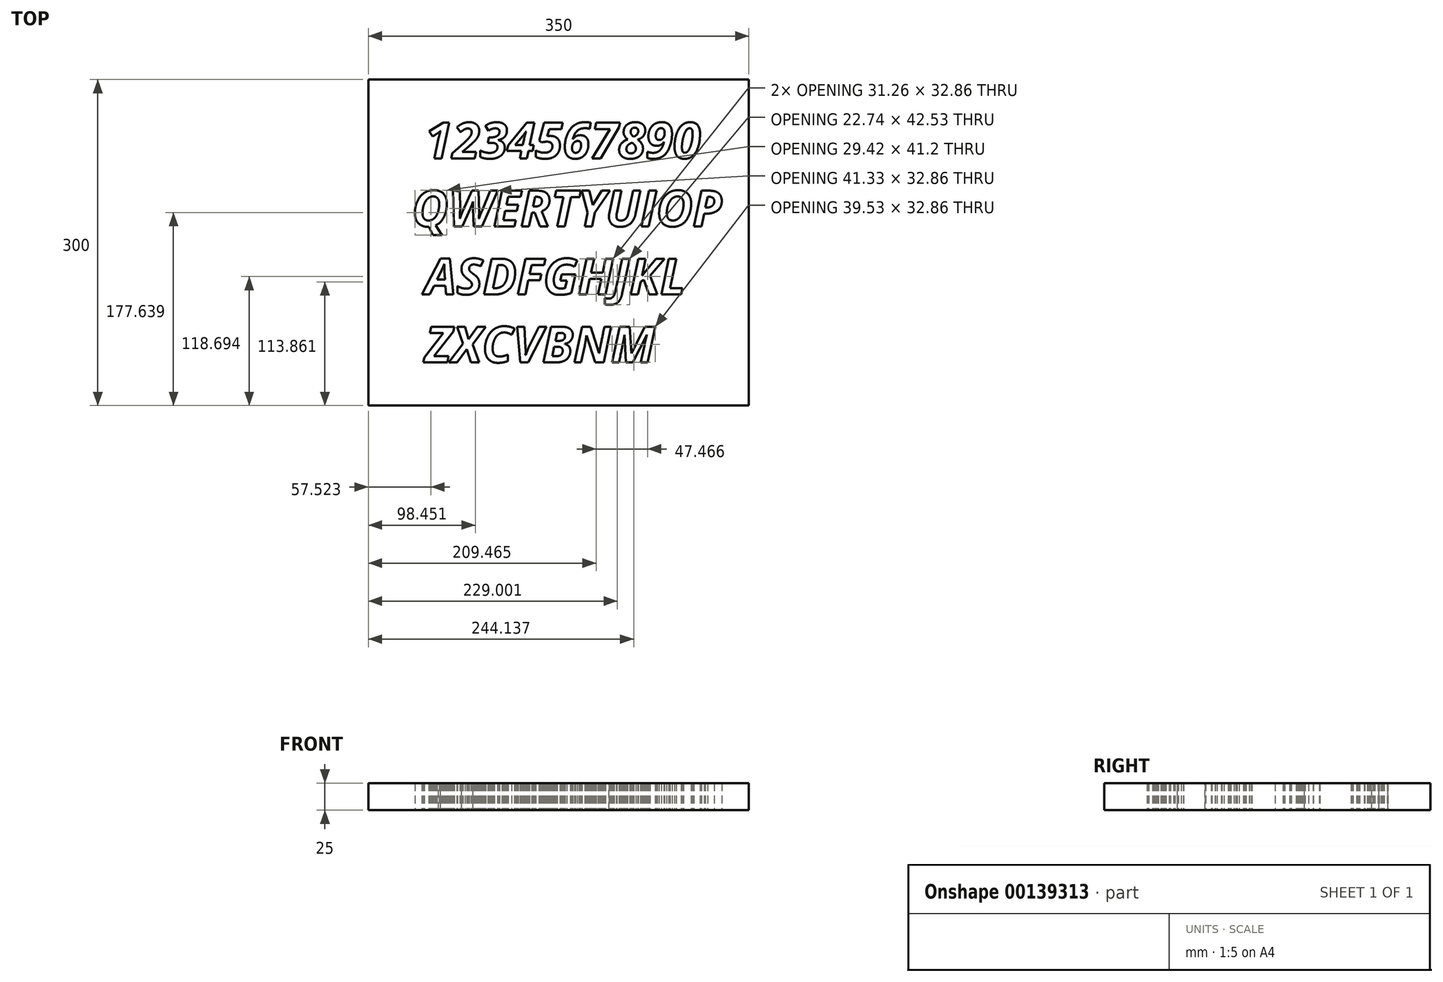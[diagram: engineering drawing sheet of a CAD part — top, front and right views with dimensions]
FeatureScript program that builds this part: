
annotation { "Feature Type Name" : "Feature", "Feature Type Description" : "" }
export const myFeature = defineFeature(function(context is Context, id is Id, definition is map)
    precondition{}
    {
        {
            var Q0;
            Q0=qCreatedBy(makeId("Top.planeOp"),FACE);
            var sketch = newSketch(context, id + "F0", { "sketchPlane" : qUnion([Q0])});
            skText(sketch, "E0", { "text": "  1234567890\n QWERTYUIOP\n  ASDFGHJKL\n  ZXCVBNM", "fontName": "OpenSans-BoldItalic.ttf"});
            const initialGuessF0  = {"E0": [-0.02613, -0.01612, 1, 0, 0.03314]};
            skSetInitialGuess(sketch, initialGuessF0);
            skSolve(sketch);
        }
        {
            var Q0;
            Q0 = qSketchRegion(id + "F0", true);
            extrude(context, id + "F1", {"entities" : qUnion([Q0]), "depth" : 25 * mm});
        }
        {
            var Q0;
            Q0=qCreatedBy(makeId("Top.planeOp"),FACE);
            var sketch = newSketch(context, id + "F2", { "sketchPlane" : qUnion([Q0])});
            skLineSegment(sketch, "E1.bottom", {"start": v(-54.22, 56.42) * mm, "end": v(295.78, 56.42) * mm});
            skLineSegment(sketch, "E1.top", {"start": v(-54.22, -243.58) * mm, "end": v(295.78, -243.58) * mm});
            skLineSegment(sketch, "E1.left", {"start": v(-54.22, 56.42) * mm, "end": v(-54.22, -243.58) * mm});
            skLineSegment(sketch, "E1.right", {"start": v(295.78, 56.42) * mm, "end": v(295.78, -243.58) * mm});
            skSolve(sketch);
        }
        {
            var Q0;
            Q0=makeQuery(id+"F2.imprint","IMPRINT",FACE,{"disambiguationData":[TD([[makeQuery(id+"F2.imprint","IMPRINT",EDGE,{"derivedFrom":sQuery(id+"F2.wireOp",EDGE,"E1.bottom")}),-1.0]])]});
            extrude(context, id + "F3", {"entities" : qUnion([Q0]), "depth" : 25 * mm});
        }
        {
            var Q0;
            Q0=makeQuery(id+"F1.opExtrude","SWEPT_BODY",BODY,{"disambiguationData":[OSD([sQuery(id+"F0.wireOp",EDGE,"E0.sketch_text.stroke-0"),sQuery(id+"F0.wireOp",EDGE,"E0.sketch_text.stroke-1"),sQuery(id+"F0.wireOp",EDGE,"E0.sketch_text.stroke-2"),sQuery(id+"F0.wireOp",EDGE,"E0.sketch_text.stroke-3"),sQuery(id+"F0.wireOp",EDGE,"E0.sketch_text.stroke-4"),sQuery(id+"F0.wireOp",EDGE,"E0.sketch_text.stroke-5"),sQuery(id+"F0.wireOp",EDGE,"E0.sketch_text.stroke-6"),sQuery(id+"F0.wireOp",EDGE,"E0.sketch_text.stroke-7"),sQuery(id+"F0.wireOp",EDGE,"E0.sketch_text.stroke-8")])]});
            var Q1;
            Q1=makeQuery(id+"F1.opExtrude","SWEPT_BODY",BODY,{"disambiguationData":[OSD([sQuery(id+"F0.wireOp",EDGE,"E0.sketch_text.stroke-9"),sQuery(id+"F0.wireOp",EDGE,"E0.sketch_text.stroke-10"),sQuery(id+"F0.wireOp",EDGE,"E0.sketch_text.stroke-11"),sQuery(id+"F0.wireOp",EDGE,"E0.sketch_text.stroke-12"),sQuery(id+"F0.wireOp",EDGE,"E0.sketch_text.stroke-13"),sQuery(id+"F0.wireOp",EDGE,"E0.sketch_text.stroke-14"),sQuery(id+"F0.wireOp",EDGE,"E0.sketch_text.stroke-15"),sQuery(id+"F0.wireOp",EDGE,"E0.sketch_text.stroke-16"),sQuery(id+"F0.wireOp",EDGE,"E0.sketch_text.stroke-17"),sQuery(id+"F0.wireOp",EDGE,"E0.sketch_text.stroke-18"),sQuery(id+"F0.wireOp",EDGE,"E0.sketch_text.stroke-19"),sQuery(id+"F0.wireOp",EDGE,"E0.sketch_text.stroke-20"),sQuery(id+"F0.wireOp",EDGE,"E0.sketch_text.stroke-21"),sQuery(id+"F0.wireOp",EDGE,"E0.sketch_text.stroke-22"),sQuery(id+"F0.wireOp",EDGE,"E0.sketch_text.stroke-23"),sQuery(id+"F0.wireOp",EDGE,"E0.sketch_text.stroke-24"),sQuery(id+"F0.wireOp",EDGE,"E0.sketch_text.stroke-25"),sQuery(id+"F0.wireOp",EDGE,"E0.sketch_text.stroke-26"),sQuery(id+"F0.wireOp",EDGE,"E0.sketch_text.stroke-27"),sQuery(id+"F0.wireOp",EDGE,"E0.sketch_text.stroke-28"),sQuery(id+"F0.wireOp",EDGE,"E0.sketch_text.stroke-29")])]});
            var Q2;
            Q2=makeQuery(id+"F1.opExtrude","SWEPT_BODY",BODY,{"disambiguationData":[OSD([sQuery(id+"F0.wireOp",EDGE,"E0.sketch_text.stroke-30"),sQuery(id+"F0.wireOp",EDGE,"E0.sketch_text.stroke-31"),sQuery(id+"F0.wireOp",EDGE,"E0.sketch_text.stroke-32"),sQuery(id+"F0.wireOp",EDGE,"E0.sketch_text.stroke-33"),sQuery(id+"F0.wireOp",EDGE,"E0.sketch_text.stroke-34"),sQuery(id+"F0.wireOp",EDGE,"E0.sketch_text.stroke-35"),sQuery(id+"F0.wireOp",EDGE,"E0.sketch_text.stroke-36"),sQuery(id+"F0.wireOp",EDGE,"E0.sketch_text.stroke-37"),sQuery(id+"F0.wireOp",EDGE,"E0.sketch_text.stroke-38"),sQuery(id+"F0.wireOp",EDGE,"E0.sketch_text.stroke-39"),sQuery(id+"F0.wireOp",EDGE,"E0.sketch_text.stroke-40"),sQuery(id+"F0.wireOp",EDGE,"E0.sketch_text.stroke-41"),sQuery(id+"F0.wireOp",EDGE,"E0.sketch_text.stroke-42"),sQuery(id+"F0.wireOp",EDGE,"E0.sketch_text.stroke-43"),sQuery(id+"F0.wireOp",EDGE,"E0.sketch_text.stroke-44"),sQuery(id+"F0.wireOp",EDGE,"E0.sketch_text.stroke-45"),sQuery(id+"F0.wireOp",EDGE,"E0.sketch_text.stroke-46"),sQuery(id+"F0.wireOp",EDGE,"E0.sketch_text.stroke-47"),sQuery(id+"F0.wireOp",EDGE,"E0.sketch_text.stroke-48"),sQuery(id+"F0.wireOp",EDGE,"E0.sketch_text.stroke-49"),sQuery(id+"F0.wireOp",EDGE,"E0.sketch_text.stroke-50"),sQuery(id+"F0.wireOp",EDGE,"E0.sketch_text.stroke-51"),sQuery(id+"F0.wireOp",EDGE,"E0.sketch_text.stroke-52"),sQuery(id+"F0.wireOp",EDGE,"E0.sketch_text.stroke-53"),sQuery(id+"F0.wireOp",EDGE,"E0.sketch_text.stroke-54"),sQuery(id+"F0.wireOp",EDGE,"E0.sketch_text.stroke-55"),sQuery(id+"F0.wireOp",EDGE,"E0.sketch_text.stroke-56"),sQuery(id+"F0.wireOp",EDGE,"E0.sketch_text.stroke-57")])]});
            var Q3;
            Q3=makeQuery(id+"F1.opExtrude","SWEPT_BODY",BODY,{"disambiguationData":[OSD([sQuery(id+"F0.wireOp",EDGE,"E0.sketch_text.stroke-58"),sQuery(id+"F0.wireOp",EDGE,"E0.sketch_text.stroke-59"),sQuery(id+"F0.wireOp",EDGE,"E0.sketch_text.stroke-60"),sQuery(id+"F0.wireOp",EDGE,"E0.sketch_text.stroke-61"),sQuery(id+"F0.wireOp",EDGE,"E0.sketch_text.stroke-62"),sQuery(id+"F0.wireOp",EDGE,"E0.sketch_text.stroke-63"),sQuery(id+"F0.wireOp",EDGE,"E0.sketch_text.stroke-64"),sQuery(id+"F0.wireOp",EDGE,"E0.sketch_text.stroke-65"),sQuery(id+"F0.wireOp",EDGE,"E0.sketch_text.stroke-66"),sQuery(id+"F0.wireOp",EDGE,"E0.sketch_text.stroke-67"),sQuery(id+"F0.wireOp",EDGE,"E0.sketch_text.stroke-68"),sQuery(id+"F0.wireOp",EDGE,"E0.sketch_text.stroke-69"),sQuery(id+"F0.wireOp",EDGE,"E0.sketch_text.stroke-70"),sQuery(id+"F0.wireOp",EDGE,"E0.sketch_text.stroke-71"),sQuery(id+"F0.wireOp",EDGE,"E0.sketch_text.stroke-72"),sQuery(id+"F0.wireOp",EDGE,"E0.sketch_text.stroke-73"),sQuery(id+"F0.wireOp",EDGE,"E0.sketch_text.stroke-74"),sQuery(id+"F0.wireOp",EDGE,"E0.sketch_text.stroke-75")])]});
            var Q4;
            Q4=makeQuery(id+"F1.opExtrude","SWEPT_BODY",BODY,{"disambiguationData":[OSD([sQuery(id+"F0.wireOp",EDGE,"E0.sketch_text.stroke-76"),sQuery(id+"F0.wireOp",EDGE,"E0.sketch_text.stroke-77"),sQuery(id+"F0.wireOp",EDGE,"E0.sketch_text.stroke-78"),sQuery(id+"F0.wireOp",EDGE,"E0.sketch_text.stroke-79"),sQuery(id+"F0.wireOp",EDGE,"E0.sketch_text.stroke-80"),sQuery(id+"F0.wireOp",EDGE,"E0.sketch_text.stroke-81"),sQuery(id+"F0.wireOp",EDGE,"E0.sketch_text.stroke-82"),sQuery(id+"F0.wireOp",EDGE,"E0.sketch_text.stroke-83"),sQuery(id+"F0.wireOp",EDGE,"E0.sketch_text.stroke-84"),sQuery(id+"F0.wireOp",EDGE,"E0.sketch_text.stroke-85"),sQuery(id+"F0.wireOp",EDGE,"E0.sketch_text.stroke-86"),sQuery(id+"F0.wireOp",EDGE,"E0.sketch_text.stroke-87"),sQuery(id+"F0.wireOp",EDGE,"E0.sketch_text.stroke-88"),sQuery(id+"F0.wireOp",EDGE,"E0.sketch_text.stroke-89"),sQuery(id+"F0.wireOp",EDGE,"E0.sketch_text.stroke-90"),sQuery(id+"F0.wireOp",EDGE,"E0.sketch_text.stroke-91"),sQuery(id+"F0.wireOp",EDGE,"E0.sketch_text.stroke-92"),sQuery(id+"F0.wireOp",EDGE,"E0.sketch_text.stroke-93"),sQuery(id+"F0.wireOp",EDGE,"E0.sketch_text.stroke-94"),sQuery(id+"F0.wireOp",EDGE,"E0.sketch_text.stroke-95"),sQuery(id+"F0.wireOp",EDGE,"E0.sketch_text.stroke-96")])]});
            var Q5;
            Q5=makeQuery(id+"F1.opExtrude","SWEPT_BODY",BODY,{"disambiguationData":[OSD([sQuery(id+"F0.wireOp",EDGE,"E0.sketch_text.stroke-97"),sQuery(id+"F0.wireOp",EDGE,"E0.sketch_text.stroke-98"),sQuery(id+"F0.wireOp",EDGE,"E0.sketch_text.stroke-99"),sQuery(id+"F0.wireOp",EDGE,"E0.sketch_text.stroke-100"),sQuery(id+"F0.wireOp",EDGE,"E0.sketch_text.stroke-101"),sQuery(id+"F0.wireOp",EDGE,"E0.sketch_text.stroke-102"),sQuery(id+"F0.wireOp",EDGE,"E0.sketch_text.stroke-103"),sQuery(id+"F0.wireOp",EDGE,"E0.sketch_text.stroke-104"),sQuery(id+"F0.wireOp",EDGE,"E0.sketch_text.stroke-105"),sQuery(id+"F0.wireOp",EDGE,"E0.sketch_text.stroke-106"),sQuery(id+"F0.wireOp",EDGE,"E0.sketch_text.stroke-107"),sQuery(id+"F0.wireOp",EDGE,"E0.sketch_text.stroke-108"),sQuery(id+"F0.wireOp",EDGE,"E0.sketch_text.stroke-109"),sQuery(id+"F0.wireOp",EDGE,"E0.sketch_text.stroke-110"),sQuery(id+"F0.wireOp",EDGE,"E0.sketch_text.stroke-111"),sQuery(id+"F0.wireOp",EDGE,"E0.sketch_text.stroke-112"),sQuery(id+"F0.wireOp",EDGE,"E0.sketch_text.stroke-113"),sQuery(id+"F0.wireOp",EDGE,"E0.sketch_text.stroke-114"),sQuery(id+"F0.wireOp",EDGE,"E0.sketch_text.stroke-115"),sQuery(id+"F0.wireOp",EDGE,"E0.sketch_text.stroke-116"),sQuery(id+"F0.wireOp",EDGE,"E0.sketch_text.stroke-117"),sQuery(id+"F0.wireOp",EDGE,"E0.sketch_text.stroke-118"),sQuery(id+"F0.wireOp",EDGE,"E0.sketch_text.stroke-119"),sQuery(id+"F0.wireOp",EDGE,"E0.sketch_text.stroke-120"),sQuery(id+"F0.wireOp",EDGE,"E0.sketch_text.stroke-121"),sQuery(id+"F0.wireOp",EDGE,"E0.sketch_text.stroke-122"),sQuery(id+"F0.wireOp",EDGE,"E0.sketch_text.stroke-123")])]});
            var Q6;
            Q6=makeQuery(id+"F1.opExtrude","SWEPT_BODY",BODY,{"disambiguationData":[OSD([sQuery(id+"F0.wireOp",EDGE,"E0.sketch_text.stroke-124"),sQuery(id+"F0.wireOp",EDGE,"E0.sketch_text.stroke-125"),sQuery(id+"F0.wireOp",EDGE,"E0.sketch_text.stroke-126"),sQuery(id+"F0.wireOp",EDGE,"E0.sketch_text.stroke-127"),sQuery(id+"F0.wireOp",EDGE,"E0.sketch_text.stroke-128"),sQuery(id+"F0.wireOp",EDGE,"E0.sketch_text.stroke-129"),sQuery(id+"F0.wireOp",EDGE,"E0.sketch_text.stroke-130")])]});
            var Q7;
            Q7=makeQuery(id+"F1.opExtrude","SWEPT_BODY",BODY,{"disambiguationData":[OSD([sQuery(id+"F0.wireOp",EDGE,"E0.sketch_text.stroke-131"),sQuery(id+"F0.wireOp",EDGE,"E0.sketch_text.stroke-132"),sQuery(id+"F0.wireOp",EDGE,"E0.sketch_text.stroke-133"),sQuery(id+"F0.wireOp",EDGE,"E0.sketch_text.stroke-134"),sQuery(id+"F0.wireOp",EDGE,"E0.sketch_text.stroke-135"),sQuery(id+"F0.wireOp",EDGE,"E0.sketch_text.stroke-136"),sQuery(id+"F0.wireOp",EDGE,"E0.sketch_text.stroke-137"),sQuery(id+"F0.wireOp",EDGE,"E0.sketch_text.stroke-138"),sQuery(id+"F0.wireOp",EDGE,"E0.sketch_text.stroke-139"),sQuery(id+"F0.wireOp",EDGE,"E0.sketch_text.stroke-140"),sQuery(id+"F0.wireOp",EDGE,"E0.sketch_text.stroke-141"),sQuery(id+"F0.wireOp",EDGE,"E0.sketch_text.stroke-142"),sQuery(id+"F0.wireOp",EDGE,"E0.sketch_text.stroke-143"),sQuery(id+"F0.wireOp",EDGE,"E0.sketch_text.stroke-144"),sQuery(id+"F0.wireOp",EDGE,"E0.sketch_text.stroke-145"),sQuery(id+"F0.wireOp",EDGE,"E0.sketch_text.stroke-146"),sQuery(id+"F0.wireOp",EDGE,"E0.sketch_text.stroke-147"),sQuery(id+"F0.wireOp",EDGE,"E0.sketch_text.stroke-148"),sQuery(id+"F0.wireOp",EDGE,"E0.sketch_text.stroke-149"),sQuery(id+"F0.wireOp",EDGE,"E0.sketch_text.stroke-150"),sQuery(id+"F0.wireOp",EDGE,"E0.sketch_text.stroke-151"),sQuery(id+"F0.wireOp",EDGE,"E0.sketch_text.stroke-152"),sQuery(id+"F0.wireOp",EDGE,"E0.sketch_text.stroke-153"),sQuery(id+"F0.wireOp",EDGE,"E0.sketch_text.stroke-154"),sQuery(id+"F0.wireOp",EDGE,"E0.sketch_text.stroke-155"),sQuery(id+"F0.wireOp",EDGE,"E0.sketch_text.stroke-156"),sQuery(id+"F0.wireOp",EDGE,"E0.sketch_text.stroke-157"),sQuery(id+"F0.wireOp",EDGE,"E0.sketch_text.stroke-158"),sQuery(id+"F0.wireOp",EDGE,"E0.sketch_text.stroke-159"),sQuery(id+"F0.wireOp",EDGE,"E0.sketch_text.stroke-160")])]});
            var Q8;
            Q8=makeQuery(id+"F1.opExtrude","SWEPT_BODY",BODY,{"disambiguationData":[OSD([sQuery(id+"F0.wireOp",EDGE,"E0.sketch_text.stroke-161"),sQuery(id+"F0.wireOp",EDGE,"E0.sketch_text.stroke-162"),sQuery(id+"F0.wireOp",EDGE,"E0.sketch_text.stroke-163"),sQuery(id+"F0.wireOp",EDGE,"E0.sketch_text.stroke-164"),sQuery(id+"F0.wireOp",EDGE,"E0.sketch_text.stroke-165"),sQuery(id+"F0.wireOp",EDGE,"E0.sketch_text.stroke-166"),sQuery(id+"F0.wireOp",EDGE,"E0.sketch_text.stroke-167"),sQuery(id+"F0.wireOp",EDGE,"E0.sketch_text.stroke-168"),sQuery(id+"F0.wireOp",EDGE,"E0.sketch_text.stroke-169"),sQuery(id+"F0.wireOp",EDGE,"E0.sketch_text.stroke-170"),sQuery(id+"F0.wireOp",EDGE,"E0.sketch_text.stroke-171"),sQuery(id+"F0.wireOp",EDGE,"E0.sketch_text.stroke-172"),sQuery(id+"F0.wireOp",EDGE,"E0.sketch_text.stroke-173"),sQuery(id+"F0.wireOp",EDGE,"E0.sketch_text.stroke-174"),sQuery(id+"F0.wireOp",EDGE,"E0.sketch_text.stroke-175"),sQuery(id+"F0.wireOp",EDGE,"E0.sketch_text.stroke-176"),sQuery(id+"F0.wireOp",EDGE,"E0.sketch_text.stroke-177"),sQuery(id+"F0.wireOp",EDGE,"E0.sketch_text.stroke-178"),sQuery(id+"F0.wireOp",EDGE,"E0.sketch_text.stroke-179"),sQuery(id+"F0.wireOp",EDGE,"E0.sketch_text.stroke-180"),sQuery(id+"F0.wireOp",EDGE,"E0.sketch_text.stroke-181"),sQuery(id+"F0.wireOp",EDGE,"E0.sketch_text.stroke-182"),sQuery(id+"F0.wireOp",EDGE,"E0.sketch_text.stroke-183"),sQuery(id+"F0.wireOp",EDGE,"E0.sketch_text.stroke-184"),sQuery(id+"F0.wireOp",EDGE,"E0.sketch_text.stroke-185"),sQuery(id+"F0.wireOp",EDGE,"E0.sketch_text.stroke-186"),sQuery(id+"F0.wireOp",EDGE,"E0.sketch_text.stroke-187"),sQuery(id+"F0.wireOp",EDGE,"E0.sketch_text.stroke-188")])]});
            var Q9;
            Q9=makeQuery(id+"F1.opExtrude","SWEPT_BODY",BODY,{"disambiguationData":[OSD([sQuery(id+"F0.wireOp",EDGE,"E0.sketch_text.stroke-189"),sQuery(id+"F0.wireOp",EDGE,"E0.sketch_text.stroke-190"),sQuery(id+"F0.wireOp",EDGE,"E0.sketch_text.stroke-191"),sQuery(id+"F0.wireOp",EDGE,"E0.sketch_text.stroke-192"),sQuery(id+"F0.wireOp",EDGE,"E0.sketch_text.stroke-193"),sQuery(id+"F0.wireOp",EDGE,"E0.sketch_text.stroke-194"),sQuery(id+"F0.wireOp",EDGE,"E0.sketch_text.stroke-195"),sQuery(id+"F0.wireOp",EDGE,"E0.sketch_text.stroke-196"),sQuery(id+"F0.wireOp",EDGE,"E0.sketch_text.stroke-197"),sQuery(id+"F0.wireOp",EDGE,"E0.sketch_text.stroke-198"),sQuery(id+"F0.wireOp",EDGE,"E0.sketch_text.stroke-199"),sQuery(id+"F0.wireOp",EDGE,"E0.sketch_text.stroke-200"),sQuery(id+"F0.wireOp",EDGE,"E0.sketch_text.stroke-201"),sQuery(id+"F0.wireOp",EDGE,"E0.sketch_text.stroke-202"),sQuery(id+"F0.wireOp",EDGE,"E0.sketch_text.stroke-203"),sQuery(id+"F0.wireOp",EDGE,"E0.sketch_text.stroke-204"),sQuery(id+"F0.wireOp",EDGE,"E0.sketch_text.stroke-205"),sQuery(id+"F0.wireOp",EDGE,"E0.sketch_text.stroke-206")])]});
            var Q10;
            Q10=makeQuery(id+"F1.opExtrude","SWEPT_BODY",BODY,{"disambiguationData":[OSD([sQuery(id+"F0.wireOp",EDGE,"E0.sketch_text.stroke-207"),sQuery(id+"F0.wireOp",EDGE,"E0.sketch_text.stroke-208"),sQuery(id+"F0.wireOp",EDGE,"E0.sketch_text.stroke-209"),sQuery(id+"F0.wireOp",EDGE,"E0.sketch_text.stroke-210"),sQuery(id+"F0.wireOp",EDGE,"E0.sketch_text.stroke-211"),sQuery(id+"F0.wireOp",EDGE,"E0.sketch_text.stroke-212"),sQuery(id+"F0.wireOp",EDGE,"E0.sketch_text.stroke-213"),sQuery(id+"F0.wireOp",EDGE,"E0.sketch_text.stroke-214"),sQuery(id+"F0.wireOp",EDGE,"E0.sketch_text.stroke-215"),sQuery(id+"F0.wireOp",EDGE,"E0.sketch_text.stroke-216"),sQuery(id+"F0.wireOp",EDGE,"E0.sketch_text.stroke-217"),sQuery(id+"F0.wireOp",EDGE,"E0.sketch_text.stroke-218"),sQuery(id+"F0.wireOp",EDGE,"E0.sketch_text.stroke-219"),sQuery(id+"F0.wireOp",EDGE,"E0.sketch_text.stroke-220"),sQuery(id+"F0.wireOp",EDGE,"E0.sketch_text.stroke-221"),sQuery(id+"F0.wireOp",EDGE,"E0.sketch_text.stroke-222"),sQuery(id+"F0.wireOp",EDGE,"E0.sketch_text.stroke-223"),sQuery(id+"F0.wireOp",EDGE,"E0.sketch_text.stroke-224"),sQuery(id+"F0.wireOp",EDGE,"E0.sketch_text.stroke-225"),sQuery(id+"F0.wireOp",EDGE,"E0.sketch_text.stroke-226"),sQuery(id+"F0.wireOp",EDGE,"E0.sketch_text.stroke-227"),sQuery(id+"F0.wireOp",EDGE,"E0.sketch_text.stroke-228"),sQuery(id+"F0.wireOp",EDGE,"E0.sketch_text.stroke-229")])]});
            var Q11;
            Q11=makeQuery(id+"F1.opExtrude","SWEPT_BODY",BODY,{"disambiguationData":[OSD([sQuery(id+"F0.wireOp",EDGE,"E0.sketch_text.stroke-230"),sQuery(id+"F0.wireOp",EDGE,"E0.sketch_text.stroke-231"),sQuery(id+"F0.wireOp",EDGE,"E0.sketch_text.stroke-232"),sQuery(id+"F0.wireOp",EDGE,"E0.sketch_text.stroke-233"),sQuery(id+"F0.wireOp",EDGE,"E0.sketch_text.stroke-234"),sQuery(id+"F0.wireOp",EDGE,"E0.sketch_text.stroke-235"),sQuery(id+"F0.wireOp",EDGE,"E0.sketch_text.stroke-236"),sQuery(id+"F0.wireOp",EDGE,"E0.sketch_text.stroke-237"),sQuery(id+"F0.wireOp",EDGE,"E0.sketch_text.stroke-238"),sQuery(id+"F0.wireOp",EDGE,"E0.sketch_text.stroke-239"),sQuery(id+"F0.wireOp",EDGE,"E0.sketch_text.stroke-240"),sQuery(id+"F0.wireOp",EDGE,"E0.sketch_text.stroke-241"),sQuery(id+"F0.wireOp",EDGE,"E0.sketch_text.stroke-242"),sQuery(id+"F0.wireOp",EDGE,"E0.sketch_text.stroke-243"),sQuery(id+"F0.wireOp",EDGE,"E0.sketch_text.stroke-244"),sQuery(id+"F0.wireOp",EDGE,"E0.sketch_text.stroke-245"),sQuery(id+"F0.wireOp",EDGE,"E0.sketch_text.stroke-246"),sQuery(id+"F0.wireOp",EDGE,"E0.sketch_text.stroke-247"),sQuery(id+"F0.wireOp",EDGE,"E0.sketch_text.stroke-248"),sQuery(id+"F0.wireOp",EDGE,"E0.sketch_text.stroke-249"),sQuery(id+"F0.wireOp",EDGE,"E0.sketch_text.stroke-250"),sQuery(id+"F0.wireOp",EDGE,"E0.sketch_text.stroke-251"),sQuery(id+"F0.wireOp",EDGE,"E0.sketch_text.stroke-252"),sQuery(id+"F0.wireOp",EDGE,"E0.sketch_text.stroke-253"),sQuery(id+"F0.wireOp",EDGE,"E0.sketch_text.stroke-254")])]});
            var Q12;
            Q12=makeQuery(id+"F1.opExtrude","SWEPT_BODY",BODY,{"disambiguationData":[OSD([sQuery(id+"F0.wireOp",EDGE,"E0.sketch_text.stroke-255"),sQuery(id+"F0.wireOp",EDGE,"E0.sketch_text.stroke-256"),sQuery(id+"F0.wireOp",EDGE,"E0.sketch_text.stroke-257"),sQuery(id+"F0.wireOp",EDGE,"E0.sketch_text.stroke-258"),sQuery(id+"F0.wireOp",EDGE,"E0.sketch_text.stroke-259"),sQuery(id+"F0.wireOp",EDGE,"E0.sketch_text.stroke-260"),sQuery(id+"F0.wireOp",EDGE,"E0.sketch_text.stroke-261"),sQuery(id+"F0.wireOp",EDGE,"E0.sketch_text.stroke-262"),sQuery(id+"F0.wireOp",EDGE,"E0.sketch_text.stroke-263"),sQuery(id+"F0.wireOp",EDGE,"E0.sketch_text.stroke-264"),sQuery(id+"F0.wireOp",EDGE,"E0.sketch_text.stroke-265"),sQuery(id+"F0.wireOp",EDGE,"E0.sketch_text.stroke-266")])]});
            var Q13;
            Q13=makeQuery(id+"F1.opExtrude","SWEPT_BODY",BODY,{"disambiguationData":[OSD([sQuery(id+"F0.wireOp",EDGE,"E0.sketch_text.stroke-267"),sQuery(id+"F0.wireOp",EDGE,"E0.sketch_text.stroke-268"),sQuery(id+"F0.wireOp",EDGE,"E0.sketch_text.stroke-269"),sQuery(id+"F0.wireOp",EDGE,"E0.sketch_text.stroke-270"),sQuery(id+"F0.wireOp",EDGE,"E0.sketch_text.stroke-271"),sQuery(id+"F0.wireOp",EDGE,"E0.sketch_text.stroke-272"),sQuery(id+"F0.wireOp",EDGE,"E0.sketch_text.stroke-273"),sQuery(id+"F0.wireOp",EDGE,"E0.sketch_text.stroke-274"),sQuery(id+"F0.wireOp",EDGE,"E0.sketch_text.stroke-275"),sQuery(id+"F0.wireOp",EDGE,"E0.sketch_text.stroke-276"),sQuery(id+"F0.wireOp",EDGE,"E0.sketch_text.stroke-277"),sQuery(id+"F0.wireOp",EDGE,"E0.sketch_text.stroke-278"),sQuery(id+"F0.wireOp",EDGE,"E0.sketch_text.stroke-279"),sQuery(id+"F0.wireOp",EDGE,"E0.sketch_text.stroke-280"),sQuery(id+"F0.wireOp",EDGE,"E0.sketch_text.stroke-281"),sQuery(id+"F0.wireOp",EDGE,"E0.sketch_text.stroke-282"),sQuery(id+"F0.wireOp",EDGE,"E0.sketch_text.stroke-283"),sQuery(id+"F0.wireOp",EDGE,"E0.sketch_text.stroke-284"),sQuery(id+"F0.wireOp",EDGE,"E0.sketch_text.stroke-285")])]});
            var Q14;
            Q14=makeQuery(id+"F1.opExtrude","SWEPT_BODY",BODY,{"disambiguationData":[OSD([sQuery(id+"F0.wireOp",EDGE,"E0.sketch_text.stroke-286"),sQuery(id+"F0.wireOp",EDGE,"E0.sketch_text.stroke-287"),sQuery(id+"F0.wireOp",EDGE,"E0.sketch_text.stroke-288"),sQuery(id+"F0.wireOp",EDGE,"E0.sketch_text.stroke-289"),sQuery(id+"F0.wireOp",EDGE,"E0.sketch_text.stroke-290"),sQuery(id+"F0.wireOp",EDGE,"E0.sketch_text.stroke-291"),sQuery(id+"F0.wireOp",EDGE,"E0.sketch_text.stroke-292"),sQuery(id+"F0.wireOp",EDGE,"E0.sketch_text.stroke-293")])]});
            var Q15;
            Q15=makeQuery(id+"F1.opExtrude","SWEPT_BODY",BODY,{"disambiguationData":[OSD([sQuery(id+"F0.wireOp",EDGE,"E0.sketch_text.stroke-294"),sQuery(id+"F0.wireOp",EDGE,"E0.sketch_text.stroke-295"),sQuery(id+"F0.wireOp",EDGE,"E0.sketch_text.stroke-296"),sQuery(id+"F0.wireOp",EDGE,"E0.sketch_text.stroke-297"),sQuery(id+"F0.wireOp",EDGE,"E0.sketch_text.stroke-298"),sQuery(id+"F0.wireOp",EDGE,"E0.sketch_text.stroke-299"),sQuery(id+"F0.wireOp",EDGE,"E0.sketch_text.stroke-300"),sQuery(id+"F0.wireOp",EDGE,"E0.sketch_text.stroke-301"),sQuery(id+"F0.wireOp",EDGE,"E0.sketch_text.stroke-302")])]});
            var Q16;
            Q16=makeQuery(id+"F1.opExtrude","SWEPT_BODY",BODY,{"disambiguationData":[OSD([sQuery(id+"F0.wireOp",EDGE,"E0.sketch_text.stroke-303"),sQuery(id+"F0.wireOp",EDGE,"E0.sketch_text.stroke-304"),sQuery(id+"F0.wireOp",EDGE,"E0.sketch_text.stroke-305"),sQuery(id+"F0.wireOp",EDGE,"E0.sketch_text.stroke-306"),sQuery(id+"F0.wireOp",EDGE,"E0.sketch_text.stroke-307"),sQuery(id+"F0.wireOp",EDGE,"E0.sketch_text.stroke-308"),sQuery(id+"F0.wireOp",EDGE,"E0.sketch_text.stroke-309"),sQuery(id+"F0.wireOp",EDGE,"E0.sketch_text.stroke-310"),sQuery(id+"F0.wireOp",EDGE,"E0.sketch_text.stroke-311"),sQuery(id+"F0.wireOp",EDGE,"E0.sketch_text.stroke-312"),sQuery(id+"F0.wireOp",EDGE,"E0.sketch_text.stroke-313"),sQuery(id+"F0.wireOp",EDGE,"E0.sketch_text.stroke-314"),sQuery(id+"F0.wireOp",EDGE,"E0.sketch_text.stroke-315"),sQuery(id+"F0.wireOp",EDGE,"E0.sketch_text.stroke-316"),sQuery(id+"F0.wireOp",EDGE,"E0.sketch_text.stroke-317")])]});
            var Q17;
            Q17=makeQuery(id+"F1.opExtrude","SWEPT_BODY",BODY,{"disambiguationData":[OSD([sQuery(id+"F0.wireOp",EDGE,"E0.sketch_text.stroke-318"),sQuery(id+"F0.wireOp",EDGE,"E0.sketch_text.stroke-319"),sQuery(id+"F0.wireOp",EDGE,"E0.sketch_text.stroke-320"),sQuery(id+"F0.wireOp",EDGE,"E0.sketch_text.stroke-321")])]});
            var Q18;
            Q18=makeQuery(id+"F1.opExtrude","SWEPT_BODY",BODY,{"disambiguationData":[OSD([sQuery(id+"F0.wireOp",EDGE,"E0.sketch_text.stroke-322"),sQuery(id+"F0.wireOp",EDGE,"E0.sketch_text.stroke-323"),sQuery(id+"F0.wireOp",EDGE,"E0.sketch_text.stroke-324"),sQuery(id+"F0.wireOp",EDGE,"E0.sketch_text.stroke-325"),sQuery(id+"F0.wireOp",EDGE,"E0.sketch_text.stroke-326"),sQuery(id+"F0.wireOp",EDGE,"E0.sketch_text.stroke-327"),sQuery(id+"F0.wireOp",EDGE,"E0.sketch_text.stroke-328"),sQuery(id+"F0.wireOp",EDGE,"E0.sketch_text.stroke-329"),sQuery(id+"F0.wireOp",EDGE,"E0.sketch_text.stroke-330"),sQuery(id+"F0.wireOp",EDGE,"E0.sketch_text.stroke-331"),sQuery(id+"F0.wireOp",EDGE,"E0.sketch_text.stroke-332"),sQuery(id+"F0.wireOp",EDGE,"E0.sketch_text.stroke-333"),sQuery(id+"F0.wireOp",EDGE,"E0.sketch_text.stroke-334"),sQuery(id+"F0.wireOp",EDGE,"E0.sketch_text.stroke-335"),sQuery(id+"F0.wireOp",EDGE,"E0.sketch_text.stroke-336"),sQuery(id+"F0.wireOp",EDGE,"E0.sketch_text.stroke-337"),sQuery(id+"F0.wireOp",EDGE,"E0.sketch_text.stroke-338"),sQuery(id+"F0.wireOp",EDGE,"E0.sketch_text.stroke-339"),sQuery(id+"F0.wireOp",EDGE,"E0.sketch_text.stroke-340"),sQuery(id+"F0.wireOp",EDGE,"E0.sketch_text.stroke-341")])]});
            var Q19;
            Q19=makeQuery(id+"F1.opExtrude","SWEPT_BODY",BODY,{"disambiguationData":[OSD([sQuery(id+"F0.wireOp",EDGE,"E0.sketch_text.stroke-342"),sQuery(id+"F0.wireOp",EDGE,"E0.sketch_text.stroke-343"),sQuery(id+"F0.wireOp",EDGE,"E0.sketch_text.stroke-344"),sQuery(id+"F0.wireOp",EDGE,"E0.sketch_text.stroke-345"),sQuery(id+"F0.wireOp",EDGE,"E0.sketch_text.stroke-346"),sQuery(id+"F0.wireOp",EDGE,"E0.sketch_text.stroke-347"),sQuery(id+"F0.wireOp",EDGE,"E0.sketch_text.stroke-348"),sQuery(id+"F0.wireOp",EDGE,"E0.sketch_text.stroke-349"),sQuery(id+"F0.wireOp",EDGE,"E0.sketch_text.stroke-350"),sQuery(id+"F0.wireOp",EDGE,"E0.sketch_text.stroke-351"),sQuery(id+"F0.wireOp",EDGE,"E0.sketch_text.stroke-352"),sQuery(id+"F0.wireOp",EDGE,"E0.sketch_text.stroke-353"),sQuery(id+"F0.wireOp",EDGE,"E0.sketch_text.stroke-354"),sQuery(id+"F0.wireOp",EDGE,"E0.sketch_text.stroke-355"),sQuery(id+"F0.wireOp",EDGE,"E0.sketch_text.stroke-356")])]});
            var Q20;
            Q20=makeQuery(id+"F1.opExtrude","SWEPT_BODY",BODY,{"disambiguationData":[OSD([sQuery(id+"F0.wireOp",EDGE,"E0.sketch_text.stroke-357"),sQuery(id+"F0.wireOp",EDGE,"E0.sketch_text.stroke-358"),sQuery(id+"F0.wireOp",EDGE,"E0.sketch_text.stroke-359"),sQuery(id+"F0.wireOp",EDGE,"E0.sketch_text.stroke-360"),sQuery(id+"F0.wireOp",EDGE,"E0.sketch_text.stroke-361"),sQuery(id+"F0.wireOp",EDGE,"E0.sketch_text.stroke-362"),sQuery(id+"F0.wireOp",EDGE,"E0.sketch_text.stroke-363"),sQuery(id+"F0.wireOp",EDGE,"E0.sketch_text.stroke-364"),sQuery(id+"F0.wireOp",EDGE,"E0.sketch_text.stroke-365"),sQuery(id+"F0.wireOp",EDGE,"E0.sketch_text.stroke-366"),sQuery(id+"F0.wireOp",EDGE,"E0.sketch_text.stroke-367"),sQuery(id+"F0.wireOp",EDGE,"E0.sketch_text.stroke-368"),sQuery(id+"F0.wireOp",EDGE,"E0.sketch_text.stroke-369"),sQuery(id+"F0.wireOp",EDGE,"E0.sketch_text.stroke-370")])]});
            var Q21;
            Q21=makeQuery(id+"F1.opExtrude","SWEPT_BODY",BODY,{"disambiguationData":[OSD([sQuery(id+"F0.wireOp",EDGE,"E0.sketch_text.stroke-371"),sQuery(id+"F0.wireOp",EDGE,"E0.sketch_text.stroke-372"),sQuery(id+"F0.wireOp",EDGE,"E0.sketch_text.stroke-373"),sQuery(id+"F0.wireOp",EDGE,"E0.sketch_text.stroke-374"),sQuery(id+"F0.wireOp",EDGE,"E0.sketch_text.stroke-375"),sQuery(id+"F0.wireOp",EDGE,"E0.sketch_text.stroke-376"),sQuery(id+"F0.wireOp",EDGE,"E0.sketch_text.stroke-377"),sQuery(id+"F0.wireOp",EDGE,"E0.sketch_text.stroke-378"),sQuery(id+"F0.wireOp",EDGE,"E0.sketch_text.stroke-379"),sQuery(id+"F0.wireOp",EDGE,"E0.sketch_text.stroke-380"),sQuery(id+"F0.wireOp",EDGE,"E0.sketch_text.stroke-381"),sQuery(id+"F0.wireOp",EDGE,"E0.sketch_text.stroke-382"),sQuery(id+"F0.wireOp",EDGE,"E0.sketch_text.stroke-383"),sQuery(id+"F0.wireOp",EDGE,"E0.sketch_text.stroke-384"),sQuery(id+"F0.wireOp",EDGE,"E0.sketch_text.stroke-385"),sQuery(id+"F0.wireOp",EDGE,"E0.sketch_text.stroke-386"),sQuery(id+"F0.wireOp",EDGE,"E0.sketch_text.stroke-387"),sQuery(id+"F0.wireOp",EDGE,"E0.sketch_text.stroke-388"),sQuery(id+"F0.wireOp",EDGE,"E0.sketch_text.stroke-389"),sQuery(id+"F0.wireOp",EDGE,"E0.sketch_text.stroke-390"),sQuery(id+"F0.wireOp",EDGE,"E0.sketch_text.stroke-391"),sQuery(id+"F0.wireOp",EDGE,"E0.sketch_text.stroke-392"),sQuery(id+"F0.wireOp",EDGE,"E0.sketch_text.stroke-393"),sQuery(id+"F0.wireOp",EDGE,"E0.sketch_text.stroke-394")])]});
            var Q22;
            Q22=makeQuery(id+"F1.opExtrude","SWEPT_BODY",BODY,{"disambiguationData":[OSD([sQuery(id+"F0.wireOp",EDGE,"E0.sketch_text.stroke-395"),sQuery(id+"F0.wireOp",EDGE,"E0.sketch_text.stroke-396"),sQuery(id+"F0.wireOp",EDGE,"E0.sketch_text.stroke-397"),sQuery(id+"F0.wireOp",EDGE,"E0.sketch_text.stroke-398"),sQuery(id+"F0.wireOp",EDGE,"E0.sketch_text.stroke-399"),sQuery(id+"F0.wireOp",EDGE,"E0.sketch_text.stroke-400"),sQuery(id+"F0.wireOp",EDGE,"E0.sketch_text.stroke-401"),sQuery(id+"F0.wireOp",EDGE,"E0.sketch_text.stroke-402"),sQuery(id+"F0.wireOp",EDGE,"E0.sketch_text.stroke-403"),sQuery(id+"F0.wireOp",EDGE,"E0.sketch_text.stroke-404"),sQuery(id+"F0.wireOp",EDGE,"E0.sketch_text.stroke-405"),sQuery(id+"F0.wireOp",EDGE,"E0.sketch_text.stroke-406"),sQuery(id+"F0.wireOp",EDGE,"E0.sketch_text.stroke-407"),sQuery(id+"F0.wireOp",EDGE,"E0.sketch_text.stroke-408"),sQuery(id+"F0.wireOp",EDGE,"E0.sketch_text.stroke-409"),sQuery(id+"F0.wireOp",EDGE,"E0.sketch_text.stroke-410")])]});
            var Q23;
            Q23=makeQuery(id+"F1.opExtrude","SWEPT_BODY",BODY,{"disambiguationData":[OSD([sQuery(id+"F0.wireOp",EDGE,"E0.sketch_text.stroke-411"),sQuery(id+"F0.wireOp",EDGE,"E0.sketch_text.stroke-412"),sQuery(id+"F0.wireOp",EDGE,"E0.sketch_text.stroke-413"),sQuery(id+"F0.wireOp",EDGE,"E0.sketch_text.stroke-414"),sQuery(id+"F0.wireOp",EDGE,"E0.sketch_text.stroke-415"),sQuery(id+"F0.wireOp",EDGE,"E0.sketch_text.stroke-416"),sQuery(id+"F0.wireOp",EDGE,"E0.sketch_text.stroke-417"),sQuery(id+"F0.wireOp",EDGE,"E0.sketch_text.stroke-418"),sQuery(id+"F0.wireOp",EDGE,"E0.sketch_text.stroke-419"),sQuery(id+"F0.wireOp",EDGE,"E0.sketch_text.stroke-420")])]});
            var Q24;
            Q24=makeQuery(id+"F1.opExtrude","SWEPT_BODY",BODY,{"disambiguationData":[OSD([sQuery(id+"F0.wireOp",EDGE,"E0.sketch_text.stroke-421"),sQuery(id+"F0.wireOp",EDGE,"E0.sketch_text.stroke-422"),sQuery(id+"F0.wireOp",EDGE,"E0.sketch_text.stroke-423"),sQuery(id+"F0.wireOp",EDGE,"E0.sketch_text.stroke-424"),sQuery(id+"F0.wireOp",EDGE,"E0.sketch_text.stroke-425"),sQuery(id+"F0.wireOp",EDGE,"E0.sketch_text.stroke-426"),sQuery(id+"F0.wireOp",EDGE,"E0.sketch_text.stroke-427"),sQuery(id+"F0.wireOp",EDGE,"E0.sketch_text.stroke-428"),sQuery(id+"F0.wireOp",EDGE,"E0.sketch_text.stroke-429"),sQuery(id+"F0.wireOp",EDGE,"E0.sketch_text.stroke-430"),sQuery(id+"F0.wireOp",EDGE,"E0.sketch_text.stroke-431"),sQuery(id+"F0.wireOp",EDGE,"E0.sketch_text.stroke-432"),sQuery(id+"F0.wireOp",EDGE,"E0.sketch_text.stroke-433"),sQuery(id+"F0.wireOp",EDGE,"E0.sketch_text.stroke-434"),sQuery(id+"F0.wireOp",EDGE,"E0.sketch_text.stroke-435"),sQuery(id+"F0.wireOp",EDGE,"E0.sketch_text.stroke-436"),sQuery(id+"F0.wireOp",EDGE,"E0.sketch_text.stroke-437"),sQuery(id+"F0.wireOp",EDGE,"E0.sketch_text.stroke-438"),sQuery(id+"F0.wireOp",EDGE,"E0.sketch_text.stroke-439"),sQuery(id+"F0.wireOp",EDGE,"E0.sketch_text.stroke-440"),sQuery(id+"F0.wireOp",EDGE,"E0.sketch_text.stroke-441"),sQuery(id+"F0.wireOp",EDGE,"E0.sketch_text.stroke-442")])]});
            var Q25;
            Q25=makeQuery(id+"F1.opExtrude","SWEPT_BODY",BODY,{"disambiguationData":[OSD([sQuery(id+"F0.wireOp",EDGE,"E0.sketch_text.stroke-443"),sQuery(id+"F0.wireOp",EDGE,"E0.sketch_text.stroke-444"),sQuery(id+"F0.wireOp",EDGE,"E0.sketch_text.stroke-445"),sQuery(id+"F0.wireOp",EDGE,"E0.sketch_text.stroke-446"),sQuery(id+"F0.wireOp",EDGE,"E0.sketch_text.stroke-447"),sQuery(id+"F0.wireOp",EDGE,"E0.sketch_text.stroke-448"),sQuery(id+"F0.wireOp",EDGE,"E0.sketch_text.stroke-449"),sQuery(id+"F0.wireOp",EDGE,"E0.sketch_text.stroke-450"),sQuery(id+"F0.wireOp",EDGE,"E0.sketch_text.stroke-451"),sQuery(id+"F0.wireOp",EDGE,"E0.sketch_text.stroke-452"),sQuery(id+"F0.wireOp",EDGE,"E0.sketch_text.stroke-453"),sQuery(id+"F0.wireOp",EDGE,"E0.sketch_text.stroke-454")])]});
            var Q26;
            Q26=makeQuery(id+"F1.opExtrude","SWEPT_BODY",BODY,{"disambiguationData":[OSD([sQuery(id+"F0.wireOp",EDGE,"E0.sketch_text.stroke-455"),sQuery(id+"F0.wireOp",EDGE,"E0.sketch_text.stroke-456"),sQuery(id+"F0.wireOp",EDGE,"E0.sketch_text.stroke-457"),sQuery(id+"F0.wireOp",EDGE,"E0.sketch_text.stroke-458"),sQuery(id+"F0.wireOp",EDGE,"E0.sketch_text.stroke-459"),sQuery(id+"F0.wireOp",EDGE,"E0.sketch_text.stroke-460"),sQuery(id+"F0.wireOp",EDGE,"E0.sketch_text.stroke-461"),sQuery(id+"F0.wireOp",EDGE,"E0.sketch_text.stroke-462"),sQuery(id+"F0.wireOp",EDGE,"E0.sketch_text.stroke-463"),sQuery(id+"F0.wireOp",EDGE,"E0.sketch_text.stroke-464")])]});
            var Q27;
            Q27=makeQuery(id+"F1.opExtrude","SWEPT_BODY",BODY,{"disambiguationData":[OSD([sQuery(id+"F0.wireOp",EDGE,"E0.sketch_text.stroke-465"),sQuery(id+"F0.wireOp",EDGE,"E0.sketch_text.stroke-466"),sQuery(id+"F0.wireOp",EDGE,"E0.sketch_text.stroke-467"),sQuery(id+"F0.wireOp",EDGE,"E0.sketch_text.stroke-468"),sQuery(id+"F0.wireOp",EDGE,"E0.sketch_text.stroke-469"),sQuery(id+"F0.wireOp",EDGE,"E0.sketch_text.stroke-470"),sQuery(id+"F0.wireOp",EDGE,"E0.sketch_text.stroke-471"),sQuery(id+"F0.wireOp",EDGE,"E0.sketch_text.stroke-472"),sQuery(id+"F0.wireOp",EDGE,"E0.sketch_text.stroke-473"),sQuery(id+"F0.wireOp",EDGE,"E0.sketch_text.stroke-474"),sQuery(id+"F0.wireOp",EDGE,"E0.sketch_text.stroke-475"),sQuery(id+"F0.wireOp",EDGE,"E0.sketch_text.stroke-476"),sQuery(id+"F0.wireOp",EDGE,"E0.sketch_text.stroke-477")])]});
            var Q28;
            Q28=makeQuery(id+"F1.opExtrude","SWEPT_BODY",BODY,{"disambiguationData":[OSD([sQuery(id+"F0.wireOp",EDGE,"E0.sketch_text.stroke-478"),sQuery(id+"F0.wireOp",EDGE,"E0.sketch_text.stroke-479"),sQuery(id+"F0.wireOp",EDGE,"E0.sketch_text.stroke-480"),sQuery(id+"F0.wireOp",EDGE,"E0.sketch_text.stroke-481"),sQuery(id+"F0.wireOp",EDGE,"E0.sketch_text.stroke-482"),sQuery(id+"F0.wireOp",EDGE,"E0.sketch_text.stroke-483")])]});
            var Q29;
            Q29=makeQuery(id+"F1.opExtrude","SWEPT_BODY",BODY,{"disambiguationData":[OSD([sQuery(id+"F0.wireOp",EDGE,"E0.sketch_text.stroke-484"),sQuery(id+"F0.wireOp",EDGE,"E0.sketch_text.stroke-485"),sQuery(id+"F0.wireOp",EDGE,"E0.sketch_text.stroke-486"),sQuery(id+"F0.wireOp",EDGE,"E0.sketch_text.stroke-487"),sQuery(id+"F0.wireOp",EDGE,"E0.sketch_text.stroke-488"),sQuery(id+"F0.wireOp",EDGE,"E0.sketch_text.stroke-489"),sQuery(id+"F0.wireOp",EDGE,"E0.sketch_text.stroke-490"),sQuery(id+"F0.wireOp",EDGE,"E0.sketch_text.stroke-491"),sQuery(id+"F0.wireOp",EDGE,"E0.sketch_text.stroke-492"),sQuery(id+"F0.wireOp",EDGE,"E0.sketch_text.stroke-493")])]});
            var Q30;
            Q30=makeQuery(id+"F1.opExtrude","SWEPT_BODY",BODY,{"disambiguationData":[OSD([sQuery(id+"F0.wireOp",EDGE,"E0.sketch_text.stroke-494"),sQuery(id+"F0.wireOp",EDGE,"E0.sketch_text.stroke-495"),sQuery(id+"F0.wireOp",EDGE,"E0.sketch_text.stroke-496"),sQuery(id+"F0.wireOp",EDGE,"E0.sketch_text.stroke-497"),sQuery(id+"F0.wireOp",EDGE,"E0.sketch_text.stroke-498"),sQuery(id+"F0.wireOp",EDGE,"E0.sketch_text.stroke-499"),sQuery(id+"F0.wireOp",EDGE,"E0.sketch_text.stroke-500"),sQuery(id+"F0.wireOp",EDGE,"E0.sketch_text.stroke-501"),sQuery(id+"F0.wireOp",EDGE,"E0.sketch_text.stroke-502"),sQuery(id+"F0.wireOp",EDGE,"E0.sketch_text.stroke-503"),sQuery(id+"F0.wireOp",EDGE,"E0.sketch_text.stroke-504"),sQuery(id+"F0.wireOp",EDGE,"E0.sketch_text.stroke-505")])]});
            var Q31;
            Q31=makeQuery(id+"F1.opExtrude","SWEPT_BODY",BODY,{"disambiguationData":[OSD([sQuery(id+"F0.wireOp",EDGE,"E0.sketch_text.stroke-506"),sQuery(id+"F0.wireOp",EDGE,"E0.sketch_text.stroke-507"),sQuery(id+"F0.wireOp",EDGE,"E0.sketch_text.stroke-508"),sQuery(id+"F0.wireOp",EDGE,"E0.sketch_text.stroke-509"),sQuery(id+"F0.wireOp",EDGE,"E0.sketch_text.stroke-510"),sQuery(id+"F0.wireOp",EDGE,"E0.sketch_text.stroke-511"),sQuery(id+"F0.wireOp",EDGE,"E0.sketch_text.stroke-512"),sQuery(id+"F0.wireOp",EDGE,"E0.sketch_text.stroke-513"),sQuery(id+"F0.wireOp",EDGE,"E0.sketch_text.stroke-514"),sQuery(id+"F0.wireOp",EDGE,"E0.sketch_text.stroke-515"),sQuery(id+"F0.wireOp",EDGE,"E0.sketch_text.stroke-516"),sQuery(id+"F0.wireOp",EDGE,"E0.sketch_text.stroke-517"),sQuery(id+"F0.wireOp",EDGE,"E0.sketch_text.stroke-518"),sQuery(id+"F0.wireOp",EDGE,"E0.sketch_text.stroke-519"),sQuery(id+"F0.wireOp",EDGE,"E0.sketch_text.stroke-520"),sQuery(id+"F0.wireOp",EDGE,"E0.sketch_text.stroke-521"),sQuery(id+"F0.wireOp",EDGE,"E0.sketch_text.stroke-522"),sQuery(id+"F0.wireOp",EDGE,"E0.sketch_text.stroke-523")])]});
            var Q32;
            Q32=makeQuery(id+"F1.opExtrude","SWEPT_BODY",BODY,{"disambiguationData":[OSD([sQuery(id+"F0.wireOp",EDGE,"E0.sketch_text.stroke-524"),sQuery(id+"F0.wireOp",EDGE,"E0.sketch_text.stroke-525"),sQuery(id+"F0.wireOp",EDGE,"E0.sketch_text.stroke-526"),sQuery(id+"F0.wireOp",EDGE,"E0.sketch_text.stroke-527"),sQuery(id+"F0.wireOp",EDGE,"E0.sketch_text.stroke-528"),sQuery(id+"F0.wireOp",EDGE,"E0.sketch_text.stroke-529"),sQuery(id+"F0.wireOp",EDGE,"E0.sketch_text.stroke-530"),sQuery(id+"F0.wireOp",EDGE,"E0.sketch_text.stroke-531"),sQuery(id+"F0.wireOp",EDGE,"E0.sketch_text.stroke-532"),sQuery(id+"F0.wireOp",EDGE,"E0.sketch_text.stroke-533"),sQuery(id+"F0.wireOp",EDGE,"E0.sketch_text.stroke-534")])]});
            var Q33;
            Q33=makeQuery(id+"F1.opExtrude","SWEPT_BODY",BODY,{"disambiguationData":[OSD([sQuery(id+"F0.wireOp",EDGE,"E0.sketch_text.stroke-535"),sQuery(id+"F0.wireOp",EDGE,"E0.sketch_text.stroke-536"),sQuery(id+"F0.wireOp",EDGE,"E0.sketch_text.stroke-537"),sQuery(id+"F0.wireOp",EDGE,"E0.sketch_text.stroke-538"),sQuery(id+"F0.wireOp",EDGE,"E0.sketch_text.stroke-539"),sQuery(id+"F0.wireOp",EDGE,"E0.sketch_text.stroke-540"),sQuery(id+"F0.wireOp",EDGE,"E0.sketch_text.stroke-541"),sQuery(id+"F0.wireOp",EDGE,"E0.sketch_text.stroke-542"),sQuery(id+"F0.wireOp",EDGE,"E0.sketch_text.stroke-543"),sQuery(id+"F0.wireOp",EDGE,"E0.sketch_text.stroke-544"),sQuery(id+"F0.wireOp",EDGE,"E0.sketch_text.stroke-545"),sQuery(id+"F0.wireOp",EDGE,"E0.sketch_text.stroke-546"),sQuery(id+"F0.wireOp",EDGE,"E0.sketch_text.stroke-547"),sQuery(id+"F0.wireOp",EDGE,"E0.sketch_text.stroke-548"),sQuery(id+"F0.wireOp",EDGE,"E0.sketch_text.stroke-549"),sQuery(id+"F0.wireOp",EDGE,"E0.sketch_text.stroke-550"),sQuery(id+"F0.wireOp",EDGE,"E0.sketch_text.stroke-551"),sQuery(id+"F0.wireOp",EDGE,"E0.sketch_text.stroke-552"),sQuery(id+"F0.wireOp",EDGE,"E0.sketch_text.stroke-553"),sQuery(id+"F0.wireOp",EDGE,"E0.sketch_text.stroke-554"),sQuery(id+"F0.wireOp",EDGE,"E0.sketch_text.stroke-555"),sQuery(id+"F0.wireOp",EDGE,"E0.sketch_text.stroke-556"),sQuery(id+"F0.wireOp",EDGE,"E0.sketch_text.stroke-557"),sQuery(id+"F0.wireOp",EDGE,"E0.sketch_text.stroke-558")])]});
            var Q34;
            Q34=makeQuery(id+"F1.opExtrude","SWEPT_BODY",BODY,{"disambiguationData":[OSD([sQuery(id+"F0.wireOp",EDGE,"E0.sketch_text.stroke-559"),sQuery(id+"F0.wireOp",EDGE,"E0.sketch_text.stroke-560"),sQuery(id+"F0.wireOp",EDGE,"E0.sketch_text.stroke-561"),sQuery(id+"F0.wireOp",EDGE,"E0.sketch_text.stroke-562"),sQuery(id+"F0.wireOp",EDGE,"E0.sketch_text.stroke-563"),sQuery(id+"F0.wireOp",EDGE,"E0.sketch_text.stroke-564"),sQuery(id+"F0.wireOp",EDGE,"E0.sketch_text.stroke-565"),sQuery(id+"F0.wireOp",EDGE,"E0.sketch_text.stroke-566"),sQuery(id+"F0.wireOp",EDGE,"E0.sketch_text.stroke-567"),sQuery(id+"F0.wireOp",EDGE,"E0.sketch_text.stroke-568"),sQuery(id+"F0.wireOp",EDGE,"E0.sketch_text.stroke-569"),sQuery(id+"F0.wireOp",EDGE,"E0.sketch_text.stroke-570"),sQuery(id+"F0.wireOp",EDGE,"E0.sketch_text.stroke-571"),sQuery(id+"F0.wireOp",EDGE,"E0.sketch_text.stroke-572"),sQuery(id+"F0.wireOp",EDGE,"E0.sketch_text.stroke-573")])]});
            var Q35;
            Q35=makeQuery(id+"F1.opExtrude","SWEPT_BODY",BODY,{"disambiguationData":[OSD([sQuery(id+"F0.wireOp",EDGE,"E0.sketch_text.stroke-574"),sQuery(id+"F0.wireOp",EDGE,"E0.sketch_text.stroke-575"),sQuery(id+"F0.wireOp",EDGE,"E0.sketch_text.stroke-576"),sQuery(id+"F0.wireOp",EDGE,"E0.sketch_text.stroke-577"),sQuery(id+"F0.wireOp",EDGE,"E0.sketch_text.stroke-578"),sQuery(id+"F0.wireOp",EDGE,"E0.sketch_text.stroke-579"),sQuery(id+"F0.wireOp",EDGE,"E0.sketch_text.stroke-580"),sQuery(id+"F0.wireOp",EDGE,"E0.sketch_text.stroke-581"),sQuery(id+"F0.wireOp",EDGE,"E0.sketch_text.stroke-582"),sQuery(id+"F0.wireOp",EDGE,"E0.sketch_text.stroke-583"),sQuery(id+"F0.wireOp",EDGE,"E0.sketch_text.stroke-584"),sQuery(id+"F0.wireOp",EDGE,"E0.sketch_text.stroke-585"),sQuery(id+"F0.wireOp",EDGE,"E0.sketch_text.stroke-586"),sQuery(id+"F0.wireOp",EDGE,"E0.sketch_text.stroke-587"),sQuery(id+"F0.wireOp",EDGE,"E0.sketch_text.stroke-588"),sQuery(id+"F0.wireOp",EDGE,"E0.sketch_text.stroke-589"),sQuery(id+"F0.wireOp",EDGE,"E0.sketch_text.stroke-590"),sQuery(id+"F0.wireOp",EDGE,"E0.sketch_text.stroke-591")])]});
            var Q36;
            Q36=makeQuery(id+"F3.opExtrude","SWEPT_BODY",BODY,{"disambiguationData":[OSD([sQuery(id+"F2.wireOp",EDGE,"E1.bottom"),sQuery(id+"F2.wireOp",EDGE,"E1.top"),sQuery(id+"F2.wireOp",EDGE,"E1.left"),sQuery(id+"F2.wireOp",EDGE,"E1.right")])]});
            booleanBodies(context, id + "F4", {"operationType" : BooleanOperationType.SUBTRACTION, "tools" : qUnion([Q0, Q1, Q2, Q3, Q4, Q5, Q6, Q7, Q8, Q9, Q10, Q11, Q12, Q13, Q14, Q15, Q16, Q17, Q18, Q19, Q20, Q21, Q22, Q23, Q24, Q25, Q26, Q27, Q28, Q29, Q30, Q31, Q32, Q33, Q34, Q35]), "targets" : qUnion([Q36])});
        }
    });
